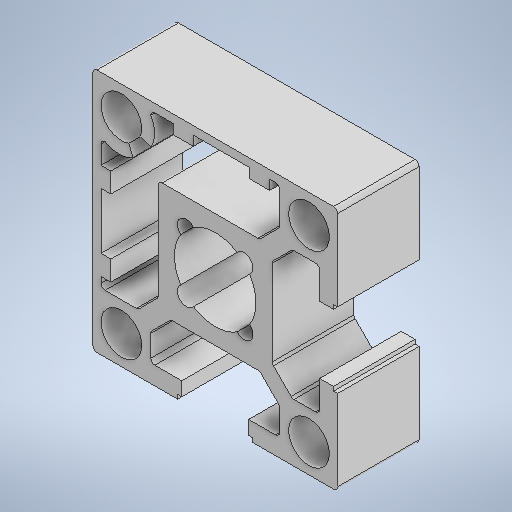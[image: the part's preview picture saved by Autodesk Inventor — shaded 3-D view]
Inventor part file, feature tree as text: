
AUTODESK INVENTOR PART (.ipt)
format: ipt  version: 2025.2 (Build 292293000, 293)  size: 419,840 bytes
history: native  units: mm
features: sketch x2, extrude x1, mirror x1
ambient origin geometry x8: Origin, YZ Plane, XZ Plane, XY Plane, X Axis, Y Axis, Z Axis, Center Point
bodies: Body1 (feature_tree)
feature tree (4):
  extrude  "Extrusão2"  Depth=30.0mm
  mirror  "Espelhar2"
  sketch  "Esboço1"  dims[d0=30.0mm d5=30.0mm]
  sketch  "Esboço - Padrão circular1"  dims[d6=15.0mm d7=10.0mm d8=8.2mm d9=8.0mm d11=2.0mm d13=0.5mm d19=5.0mm d23=1.1mm d26=11.5mm d27=2.2mm d28=1.1mm d29=1.1mm d33=2.2mm d34=2.2mm d35=40.0mm d37=360.0deg d39=1.1mm d44=10.0mm d45=0.0mm d46=0.0mm d47=0.0mm d48=0.0mm d49=0.0mm]
